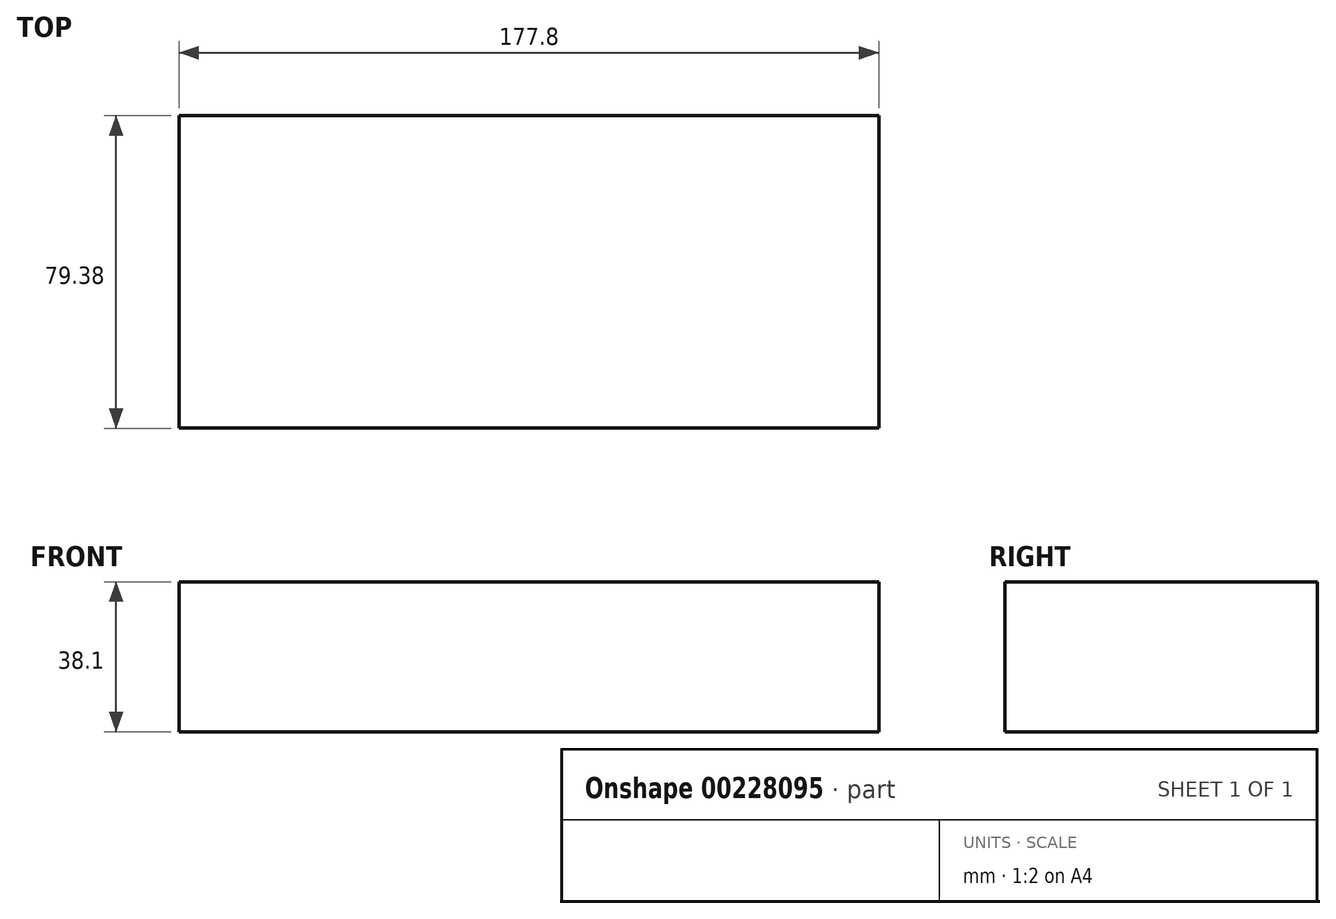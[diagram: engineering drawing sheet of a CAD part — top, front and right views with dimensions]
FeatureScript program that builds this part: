
annotation { "Feature Type Name" : "Feature", "Feature Type Description" : "" }
export const myFeature = defineFeature(function(context is Context, id is Id, definition is map)
    precondition{}
    {
        {
            var Q0;
            Q0=qCreatedBy(makeId("Front.planeOp"),FACE);
            var sketch = newSketch(context, id + "F0", { "sketchPlane" : qUnion([Q0])});
            skLineSegment(sketch, "E0.bottom", {"start": v(88.9, -19.05) * mm, "end": v(-88.9, -19.05) * mm});
            skLineSegment(sketch, "E0.top", {"start": v(88.9, 19.05) * mm, "end": v(-88.9, 19.05) * mm});
            skLineSegment(sketch, "E0.left", {"start": v(88.9, -19.05) * mm, "end": v(88.9, 19.05) * mm});
            skLineSegment(sketch, "E0.right", {"start": v(-88.9, -19.05) * mm, "end": v(-88.9, 19.05) * mm});
            skPoint(sketch, "E0.middle", {"position": v(0, 0) * mm});
            skLineSegment(sketch, "E1", {"start": v(-89.87, -26.04) * mm, "end": v(87.93, -26.04) * mm, "construction": true});
            skCircle(sketch, "E2", {"center": v(63.5, -5.08) * mm, "radius": 20.96 * mm});
            skSolve(sketch);
        }
        {
            var Q0;
            Q0=qCreatedBy(makeId("Front.planeOp"),FACE);
            var sketch = newSketch(context, id + "F1", { "sketchPlane" : qUnion([Q0])});
            skLineSegment(sketch, "E3.0", {"start": v(-88.9, -19.05) * mm, "end": v(-88.9, 19.05) * mm});
            skLineSegment(sketch, "E4.0", {"start": v(88.9, 19.05) * mm, "end": v(-88.9, 19.05) * mm});
            skLineSegment(sketch, "E5.0", {"start": v(88.9, -19.05) * mm, "end": v(-88.9, -19.05) * mm});
            skLineSegment(sketch, "E6.0", {"start": v(88.9, -19.05) * mm, "end": v(88.9, 19.05) * mm});
            skSolve(sketch);
        }
        {
            var Q0;
            Q0 = qSketchRegion(id + "F1", true);
            extrude(context, id + "F2", {"entities" : qUnion([Q0]), "endBound" : BoundingType.SYMMETRIC, "depth" : 79.38 * mm});
        }
    });
